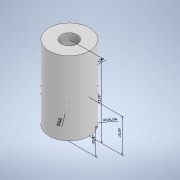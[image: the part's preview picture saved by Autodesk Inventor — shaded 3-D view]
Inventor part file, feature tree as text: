
AUTODESK INVENTOR PART (.ipt)
format: ipt  version: 2021.2 (Build 252289000, 289)  size: 145,920 bytes
history: native  units: mm
features: other x10, sketch x4, extrude x2, hole x2, thread x1
ambient origin geometry x8: Origin, YZ Plane, XZ Plane, XY Plane, X Axis, Y Axis, Z Axis, Center Point
bodies: Body1 (feature_tree)
feature tree (19):
  other  "Твердое тело1"
  other  "Аннотации"
  extrude  "Выдавливание1"  Depth=30.0mm
  other  "РабПлоскость1"
  hole  "Отверстие2"  [1 undecoded]
  other  "РабПлоскость2"
  hole  "Отверстие3"  [1 undecoded]
  extrude  "Выдавливание2"  Depth=20.0mm TaperAngle=0.0deg
  thread  "Резьба1"
  sketch  "Эскиз1"
  sketch  "Эскиз5"
  sketch  "Эскиз6"
  sketch  "Эскиз7"
  other  "Линейный размер 1"
  other  "Линейный размер 2"
  other  "Диаметр 1"
  other  "Диаметр 2"
  other  "Диаметр 3"
  other  "Линейный размер 3"
note: 2 required parameter values undecoded (feature->parameter linkage not recoverable at this tier; creation-order binding heuristic only, values carry confidence <= 0.55)
